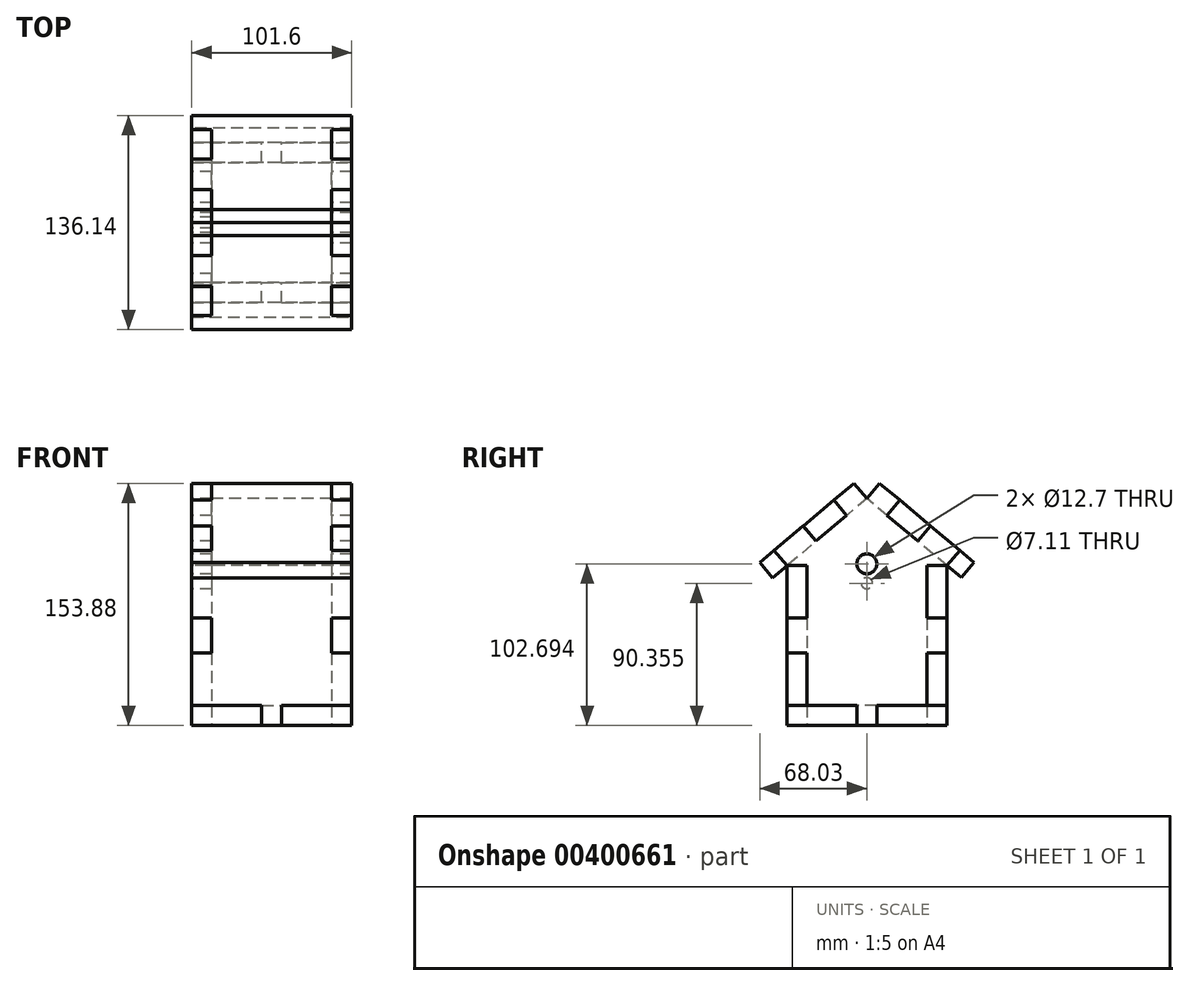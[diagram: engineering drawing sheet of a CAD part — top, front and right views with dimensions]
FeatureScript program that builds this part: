
annotation { "Feature Type Name" : "Feature", "Feature Type Description" : "" }
export const myFeature = defineFeature(function(context is Context, id is Id, definition is map)
    precondition{}
    {
        {
            var Q0;
            Q0=qCreatedBy(makeId("Top.planeOp"),FACE);
            var sketch = newSketch(context, id + "F0", { "sketchPlane" : qUnion([Q0])});
            skLineSegment(sketch, "E0.bottom", {"start": v(-50.8, 50.8) * mm, "end": v(-6.35, 50.8) * mm});
            skLineSegment(sketch, "E0.top", {"start": v(-50.8, -50.8) * mm, "end": v(-6.35, -50.8) * mm});
            skLineSegment(sketch, "E0.left", {"start": v(-50.8, 50.8) * mm, "end": v(-50.8, 6.35) * mm});
            skLineSegment(sketch, "E0.right", {"start": v(50.8, 50.8) * mm, "end": v(50.8, 6.35) * mm});
            skPoint(sketch, "E0.middle", {"position": v(0, 0) * mm});
            skLineSegment(sketch, "E1", {"start": v(-50.8, 6.35) * mm, "end": v(-38.1, 6.35) * mm});
            skLineSegment(sketch, "E2", {"start": v(-38.1, 6.35) * mm, "end": v(-38.1, -6.35) * mm});
            skLineSegment(sketch, "E3", {"start": v(-50.8, -6.35) * mm, "end": v(-38.1, -6.35) * mm});
            skLineSegment(sketch, "E4.trimOffspring", {"start": v(-50.8, -6.35) * mm, "end": v(-50.8, -50.8) * mm});
            skLineSegment(sketch, "E5.MirrorCS", {"start": v(50.8, 6.35) * mm, "end": v(38.1, 6.35) * mm});
            skLineSegment(sketch, "E6.MirrorCS", {"start": v(38.1, 6.35) * mm, "end": v(38.1, -6.35) * mm});
            skLineSegment(sketch, "E7.MirrorCS", {"start": v(50.8, -6.35) * mm, "end": v(38.1, -6.35) * mm});
            skLineSegment(sketch, "E8.trimOffspring", {"start": v(50.8, -6.35) * mm, "end": v(50.8, -50.8) * mm});
            skLineSegment(sketch, "E9", {"start": v(-6.35, 50.8) * mm, "end": v(-6.35, 38.1) * mm});
            skLineSegment(sketch, "E10", {"start": v(6.35, 50.8) * mm, "end": v(6.35, 38.1) * mm});
            skLineSegment(sketch, "E11", {"start": v(-6.35, 38.1) * mm, "end": v(6.35, 38.1) * mm});
            skLineSegment(sketch, "E12.trimOffspring", {"start": v(6.35, 50.8) * mm, "end": v(50.8, 50.8) * mm});
            skLineSegment(sketch, "E13.MirrorCS", {"start": v(-6.35, -38.1) * mm, "end": v(6.35, -38.1) * mm});
            skLineSegment(sketch, "E14.MirrorCS", {"start": v(-6.35, -50.8) * mm, "end": v(-6.35, -38.1) * mm});
            skLineSegment(sketch, "E15.MirrorCS", {"start": v(6.35, -50.8) * mm, "end": v(6.35, -38.1) * mm});
            skLineSegment(sketch, "E16.trimOffspring", {"start": v(6.35, -50.8) * mm, "end": v(50.8, -50.8) * mm});
            skSolve(sketch);
        }
        {
            var Q0;
            Q0 = qSketchRegion(id + "F0", true);
            extrude(context, id + "F1", {"entities" : qUnion([Q0]), "depth" : 12.7 * mm});
        }
        {
            var Q0;
            Q0=makeQuery(id+"F1.opExtrude","SWEPT_FACE",FACE,{"disambiguationData":[OSD([sQuery(id+"F0.wireOp",EDGE,"E12.trimOffspring")])]});
            var sketch = newSketch(context, id + "F2", { "sketchPlane" : qUnion([Q0])});
            skLineSegment(sketch, "E17.bottom", {"start": v(-6.35, 0) * mm, "end": v(6.35, 0) * mm});
            skLineSegment(sketch, "E17.top", {"start": v(-50.8, 101.6) * mm, "end": v(-12.84, 101.6) * mm});
            skLineSegment(sketch, "E17.right", {"start": v(50.8, 12.7) * mm, "end": v(50.8, 46.04) * mm});
            skLineSegment(sketch, "E18", {"start": v(-6.35, 0) * mm, "end": v(-6.35, 12.7) * mm});
            skLineSegment(sketch, "E19", {"start": v(6.35, 12.7) * mm, "end": v(6.35, 0) * mm});
            skLineSegment(sketch, "E20", {"start": v(51.45, 0) * mm, "end": v(-50.8, 0) * mm});
            skLineSegment(sketch, "E21", {"start": v(-50.8, 101.6) * mm, "end": v(-50.8, 68.26) * mm});
            skLineSegment(sketch, "E22", {"start": v(-50.8, 12.7) * mm, "end": v(-50.8, 46.04) * mm});
            skLineSegment(sketch, "E23", {"start": v(-50.8, 68.26) * mm, "end": v(-38.1, 68.26) * mm});
            skLineSegment(sketch, "E24", {"start": v(-38.1, 68.26) * mm, "end": v(-38.1, 46.04) * mm});
            skLineSegment(sketch, "E25", {"start": v(-50.8, 46.04) * mm, "end": v(-38.1, 46.04) * mm});
            skLineSegment(sketch, "E26.MirrorCS", {"start": v(50.8, 68.26) * mm, "end": v(38.1, 68.26) * mm});
            skLineSegment(sketch, "E27.MirrorCS", {"start": v(38.1, 68.26) * mm, "end": v(38.1, 46.04) * mm});
            skLineSegment(sketch, "E28.MirrorCS", {"start": v(50.8, 46.04) * mm, "end": v(38.1, 46.04) * mm});
            skLineSegment(sketch, "E29.trimOffspring", {"start": v(50.8, 68.26) * mm, "end": v(50.8, 101.6) * mm});
            skLineSegment(sketch, "E30", {"start": v(-50.8, 12.7) * mm, "end": v(-6.35, 12.7) * mm});
            skLineSegment(sketch, "E31", {"start": v(50.8, 12.7) * mm, "end": v(6.35, 12.7) * mm});
            skLineSegment(sketch, "E32", {"start": v(50.8, 101.6) * mm, "end": v(12.7, 101.6) * mm});
            skLineSegment(sketch, "E33", {"start": v(-12.84, 101.6) * mm, "end": v(-12.84, 88.9) * mm});
            skLineSegment(sketch, "E34", {"start": v(-12.84, 88.9) * mm, "end": v(12.7, 88.9) * mm});
            skLineSegment(sketch, "E35", {"start": v(12.7, 101.6) * mm, "end": v(12.7, 88.9) * mm});
            skLineSegment(sketch, "E36.trimOffspring", {"start": v(12.7, 101.6) * mm, "end": v(50.8, 101.6) * mm});
            skLineSegment(sketch, "E37", {"start": v(-12.84, 101.6) * mm, "end": v(12.7, 101.6) * mm});
            skSolve(sketch);
        }
        {
            var Q0;
            Q0 = qSketchRegion(id + "F2", true);
            var Q1;
            Q1=makeQuery(id+"F2.imprint","IMPRINT",FACE,{"disambiguationData":[TD([[makeQuery(id+"F2.imprint","IMPRINT",EDGE,{"derivedFrom":sQuery(id+"F2.wireOp",EDGE,"E17.top")}),-1.0]])]});
            extrude(context, id + "F3", {"entities" : qUnion([Q0, Q1]), "oppositeDirection" : true, "depth" : 12.7 * mm});
        }
        {
            var Q0;
            Q0=makeQuery(id+"F1.opExtrude","SWEPT_FACE",FACE,{"disambiguationData":[OSD([sQuery(id+"F0.wireOp",EDGE,"E4.trimOffspring")])]});
            var sketch = newSketch(context, id + "F4", { "sketchPlane" : qUnion([Q0])});
            skLineSegment(sketch, "E38", {"start": v(-38.1, 101.6) * mm, "end": v(-38.1, 68.26) * mm});
            skLineSegment(sketch, "E39", {"start": v(-50.8, 46.04) * mm, "end": v(-38.1, 46.04) * mm});
            skLineSegment(sketch, "E40", {"start": v(-38.1, 46.04) * mm, "end": v(-38.1, 12.7) * mm});
            skLineSegment(sketch, "E41", {"start": v(-38.1, 12.7) * mm, "end": v(-6.35, 12.7) * mm});
            skLineSegment(sketch, "E42", {"start": v(-6.35, 12.7) * mm, "end": v(-6.35, 0) * mm});
            skLineSegment(sketch, "E43", {"start": v(-6.35, 0) * mm, "end": v(6.35, 0) * mm});
            skLineSegment(sketch, "E44", {"start": v(6.35, 12.7) * mm, "end": v(6.35, 0) * mm});
            skLineSegment(sketch, "E45", {"start": v(6.35, 12.7) * mm, "end": v(50.8, 12.7) * mm});
            skLineSegment(sketch, "E46.MirrorCS", {"start": v(37.98, 68.26) * mm, "end": v(50.68, 68.26) * mm});
            skLineSegment(sketch, "E47.MirrorCS", {"start": v(50.8, 46.04) * mm, "end": v(38.1, 46.04) * mm});
            skLineSegment(sketch, "E48", {"start": v(38.1, 46.04) * mm, "end": v(38.1, 12.7) * mm});
            skLineSegment(sketch, "E49", {"start": v(-38.1, 68.26) * mm, "end": v(-38.1, 101.6) * mm});
            skLineSegment(sketch, "E50", {"start": v(-50.8, 68.26) * mm, "end": v(-38.1, 68.26) * mm});
            skLineSegment(sketch, "E51", {"start": v(-50.8, 68.26) * mm, "end": v(-50.8, 46.04) * mm});
            skLineSegment(sketch, "E52", {"start": v(50.8, 46.04) * mm, "end": v(50.68, 68.26) * mm});
            skLineSegment(sketch, "E53", {"start": v(38.1, 101.6) * mm, "end": v(37.98, 68.26) * mm});
            skCircle(sketch, "E54", {"center": v(0, 102.7) * mm, "radius": 6.35 * mm});
            skLineSegment(sketch, "E55", {"start": v(12.84, 133.39) * mm, "end": v(32.31, 117.08) * mm});
            skLineSegment(sketch, "E56.MirrorCS", {"start": v(-12.84, 133.39) * mm, "end": v(-32.31, 117.08) * mm});
            skLineSegment(sketch, "E57", {"start": v(38.1, 101.6) * mm, "end": v(50.8, 101.6) * mm});
            skLineSegment(sketch, "E58", {"start": v(-50.8, 101.6) * mm, "end": v(-38.1, 101.6) * mm});
            skLineSegment(sketch, "E59.0", {"start": v(-40.47, 126.82) * mm, "end": v(-58.95, 111.34) * mm});
            skLineSegment(sketch, "E59.1", {"start": v(-21, 143.13) * mm, "end": v(-8.15, 153.88) * mm});
            skLineSegment(sketch, "E59.2", {"start": v(21, 143.13) * mm, "end": v(8.15, 153.88) * mm});
            skLineSegment(sketch, "E59.3", {"start": v(40.47, 126.82) * mm, "end": v(58.95, 111.34) * mm});
            skLineSegment(sketch, "E60", {"start": v(-21, 143.13) * mm, "end": v(-12.84, 133.39) * mm});
            skLineSegment(sketch, "E61.0", {"start": v(-40.47, 126.82) * mm, "end": v(-32.31, 117.08) * mm});
            skLineSegment(sketch, "E62", {"start": v(-58.95, 111.34) * mm, "end": v(-50.8, 101.6) * mm});
            skLineSegment(sketch, "E63", {"start": v(0, 144.14) * mm, "end": v(-8.15, 153.88) * mm});
            skLineSegment(sketch, "E64.MirrorCS", {"start": v(0, 144.14) * mm, "end": v(8.15, 153.88) * mm});
            skLineSegment(sketch, "E65.MirrorCS", {"start": v(21, 143.13) * mm, "end": v(12.84, 133.39) * mm});
            skLineSegment(sketch, "E66.MirrorCS", {"start": v(40.47, 126.82) * mm, "end": v(32.31, 117.08) * mm});
            skLineSegment(sketch, "E67.MirrorCS", {"start": v(58.95, 111.34) * mm, "end": v(50.8, 101.6) * mm});
            skSolve(sketch);
        }
        {
            var Q0;
            Q0=makeQuery(id+"F4.imprint","IMPRINT",FACE,{"disambiguationData":[TD([[makeQuery(id+"F4.imprint","IMPRINT",EDGE,{"derivedFrom":sQuery(id+"F4.wireOp",EDGE,"E39")}),1.0]])]});
            extrude(context, id + "F5", {"entities" : qUnion([Q0]), "oppositeDirection" : true, "depth" : 12.7 * mm});
        }
        {
            var Q0;
            Q0=makeQuery(id+"F5.opExtrude","SWEPT_BODY",BODY,{"disambiguationData":[OSD([sQuery(id+"F4.wireOp",EDGE,"E38"),sQuery(id+"F4.wireOp",EDGE,"X9XSPmUe-CiWI-aoBv-T2po-TQAexjn7eybI"),sQuery(id+"F4.wireOp",EDGE,"dJrmhynW-Dqij-QMza-xG0c-FiWTCxEsIYWA"),sQuery(id+"F4.wireOp",EDGE,"E39"),sQuery(id+"F4.wireOp",EDGE,"E40"),sQuery(id+"F4.wireOp",EDGE,"E41"),sQuery(id+"F4.wireOp",EDGE,"E42"),sQuery(id+"F4.wireOp",EDGE,"E43"),sQuery(id+"F4.wireOp",EDGE,"E44"),sQuery(id+"F4.wireOp",EDGE,"E45"),sQuery(id+"F4.wireOp",EDGE,"E46.MirrorCS"),sQuery(id+"F4.wireOp",EDGE,"E47.MirrorCS"),sQuery(id+"F4.wireOp",EDGE,"7d2038e0-95e8-4499-a10f-d84e647bfb870.MirrorCS"),sQuery(id+"F4.wireOp",EDGE,"3vYFP86l-RaxW-OtnJ-uWa2-55M71DUzLll7"),sQuery(id+"F4.wireOp",EDGE,"E48"),sQuery(id+"F4.wireOp",EDGE,"Zbu0z1yX-9y8x-yxQX-ajQ6-gNSLApIAPJhn"),sQuery(id+"F4.wireOp",EDGE,"R7JFiNgy-TADh-oWcj-84EZ-rrNiW4IfCNvZ"),sQuery(id+"F4.wireOp",EDGE,"B0p03boq-Z1hu-uY6q-z4ZI-CZ741v1NlHqN"),sQuery(id+"F4.wireOp",EDGE,"oFCeFuHr-h53X-c4xK-BUlm-Z66OJnlluKQs"),sQuery(id+"F4.wireOp",EDGE,"795be2b4-63bf-446e-84a7-18ad7f5d247d.trimOffspring")])]});
            var Q1;
            Q1=makeQuery(id+"F5.opExtrude","CAP_VERTEX",VERTEX,{"disambiguationData":[OSD([sQuery(id+"F4.wireOp",EDGE,"E41"),sQuery(id+"F4.wireOp",EDGE,"E42")])],"isStart":false});
            var Q2;
            Q2=makeQuery(id+"F1.opExtrude","CAP_VERTEX",VERTEX,{"disambiguationData":[OSD([sQuery(id+"F0.wireOp",EDGE,"E0.right"),sQuery(id+"F0.wireOp",EDGE,"E5.MirrorCS")])],"isStart":false});
            transform(context, id + "F6", {"entities" : qUnion([Q0]), "transformType" : TransformType.TRANSLATION_ENTITY, "oppositeDirectionEntity" : false, "transformLine" : qUnion([Q1, Q2]), "makeCopy" : true});
        }
        {
            var Q0;
            Q0=makeQuery(id+"F3.opExtrude","SWEPT_BODY",BODY,{"disambiguationData":[OSD([sQuery(id+"F2.wireOp",EDGE,"E17.right"),sQuery(id+"F2.wireOp",EDGE,"E18"),sQuery(id+"F2.wireOp",EDGE,"E19"),sQuery(id+"F2.wireOp",EDGE,"E20"),sQuery(id+"F2.wireOp",EDGE,"E21"),sQuery(id+"F2.wireOp",EDGE,"E22"),sQuery(id+"F2.wireOp",EDGE,"E23"),sQuery(id+"F2.wireOp",EDGE,"E24"),sQuery(id+"F2.wireOp",EDGE,"E25"),sQuery(id+"F2.wireOp",EDGE,"E26.MirrorCS"),sQuery(id+"F2.wireOp",EDGE,"E27.MirrorCS"),sQuery(id+"F2.wireOp",EDGE,"E28.MirrorCS"),sQuery(id+"F2.wireOp",EDGE,"E29.trimOffspring"),sQuery(id+"F2.wireOp",EDGE,"E30"),sQuery(id+"F2.wireOp",EDGE,"E31"),sQuery(id+"F2.wireOp",EDGE,"E17.top"),sQuery(id+"F2.wireOp",EDGE,"E33"),sQuery(id+"F2.wireOp",EDGE,"E34"),sQuery(id+"F2.wireOp",EDGE,"E35"),sQuery(id+"F2.wireOp",EDGE,"E36.trimOffspring")])]});
            var Q1;
            Q1=makeQuery(id+"F1.opExtrude","CAP_VERTEX",VERTEX,{"disambiguationData":[OSD([sQuery(id+"F0.wireOp",EDGE,"E10"),sQuery(id+"F0.wireOp",EDGE,"E11")])],"isStart":false});
            var Q2;
            Q2=makeQuery(id+"F1.opExtrude","CAP_VERTEX",VERTEX,{"disambiguationData":[OSD([sQuery(id+"F0.wireOp",EDGE,"E15.MirrorCS"),sQuery(id+"F0.wireOp",EDGE,"E16.trimOffspring")])],"isStart":false});
            transform(context, id + "F7", {"entities" : qUnion([Q0]), "transformType" : TransformType.TRANSLATION_ENTITY, "oppositeDirectionEntity" : false, "transformLine" : qUnion([Q1, Q2]), "makeCopy" : true});
        }
        {
            var Q0;
            Q0=makeQuery(id+"F6.opPattern","COPY",FACE,{"derivedFrom":makeQuery(id+"F5.opExtrude","SWEPT_FACE",FACE,{"disambiguationData":[OSD([sQuery(id+"F4.wireOp",EDGE,"E56.MirrorCS")])]}),"instanceName":"1"});
            var sketch = newSketch(context, id + "F8", { "sketchPlane" : qUnion([Q0])});
            skLineSegment(sketch, "E68.bottom", {"start": v(50.8, -14.34) * mm, "end": v(-50.8, -14.34) * mm});
            skLineSegment(sketch, "E68.top", {"start": v(50.8, -92.54) * mm, "end": v(-50.8, -92.54) * mm});
            skLineSegment(sketch, "E68.left", {"start": v(50.8, -14.34) * mm, "end": v(50.8, -92.54) * mm});
            skLineSegment(sketch, "E68.right", {"start": v(-50.8, -14.34) * mm, "end": v(-50.8, -92.54) * mm});
            skSolve(sketch);
        }
        {
            var Q0;
            Q0 = qSketchRegion(id + "F8", true);
            extrude(context, id + "F9", {"entities" : qUnion([Q0]), "depth" : 12.7 * mm});
        }
        {
            var Q0;
            Q0=makeQuery(id+"F9.opExtrude","SWEPT_BODY",BODY,{"disambiguationData":[OSD([sQuery(id+"F8.wireOp",EDGE,"E68.bottom"),sQuery(id+"F8.wireOp",EDGE,"E68.top"),sQuery(id+"F8.wireOp",EDGE,"E68.left"),sQuery(id+"F8.wireOp",EDGE,"E68.right")])]});
            var Q1;
            Q1=sQuery(id+"F4.wireOp",EDGE,"E63");
            transform(context, id + "F10", {"entities" : qUnion([Q0]), "transformType" : TransformType.ROTATION, "transformAxis" : qUnion([Q1]), "angle" : 180 * degree, "makeCopy" : true});
        }
        {
            var Q0;
            Q0=makeQuery(id+"F10.opPattern","COPY",BODY,{"derivedFrom":makeQuery(id+"F9.opExtrude","SWEPT_BODY",BODY,{"disambiguationData":[OSD([sQuery(id+"F8.wireOp",EDGE,"E68.bottom"),sQuery(id+"F8.wireOp",EDGE,"E68.top"),sQuery(id+"F8.wireOp",EDGE,"E68.left"),sQuery(id+"F8.wireOp",EDGE,"E68.right")])]}),"instanceName":"1"});
            var Q1;
            Q1=makeQuery(id+"F10.opPattern","COPY",EDGE,{"derivedFrom":makeQuery(id+"F9.opExtrude","CAP_EDGE",EDGE,{"disambiguationData":[OSD([sQuery(id+"F8.wireOp",EDGE,"E68.top")])],"isStart":true}),"instanceName":"1"});
            transform(context, id + "F11", {"entities" : qUnion([Q0]), "transformType" : TransformType.ROTATION, "transformAxis" : qUnion([Q1]), "angle" : 80 * degree, "makeCopy" : false});
        }
        {
            var Q0;
            Q0=makeQuery(id+"F10.opPattern","COPY",BODY,{"derivedFrom":makeQuery(id+"F9.opExtrude","SWEPT_BODY",BODY,{"disambiguationData":[OSD([sQuery(id+"F8.wireOp",EDGE,"E68.bottom"),sQuery(id+"F8.wireOp",EDGE,"E68.top"),sQuery(id+"F8.wireOp",EDGE,"E68.left"),sQuery(id+"F8.wireOp",EDGE,"E68.right")])]}),"instanceName":"1"});
            var Q1;
            Q1=makeQuery(id+"F9.opExtrude","CAP_EDGE",EDGE,{"disambiguationData":[OSD([sQuery(id+"F8.wireOp",EDGE,"E68.top")])],"isStart":true});
            transform(context, id + "F12", {"entities" : qUnion([Q0]), "transformType" : TransformType.TRANSLATION_ENTITY, "oppositeDirectionEntity" : true, "transformLine" : qUnion([Q1]), "makeCopy" : false});
        }
        {
            var Q0;
            Q0=makeQuery(id+"F5.opExtrude","SWEPT_BODY",BODY,{"disambiguationData":[OSD([sQuery(id+"F4.wireOp",EDGE,"E39"),sQuery(id+"F4.wireOp",EDGE,"E40"),sQuery(id+"F4.wireOp",EDGE,"E41"),sQuery(id+"F4.wireOp",EDGE,"E42"),sQuery(id+"F4.wireOp",EDGE,"E43"),sQuery(id+"F4.wireOp",EDGE,"E44"),sQuery(id+"F4.wireOp",EDGE,"E45"),sQuery(id+"F4.wireOp",EDGE,"E46.MirrorCS"),sQuery(id+"F4.wireOp",EDGE,"E47.MirrorCS"),sQuery(id+"F4.wireOp",EDGE,"E48"),sQuery(id+"F4.wireOp",EDGE,"E49"),sQuery(id+"F4.wireOp",EDGE,"E50"),sQuery(id+"F4.wireOp",EDGE,"E51"),sQuery(id+"F4.wireOp",EDGE,"E52"),sQuery(id+"F4.wireOp",EDGE,"E53"),sQuery(id+"F4.wireOp",EDGE,"E54"),sQuery(id+"F4.wireOp",EDGE,"E55"),sQuery(id+"F4.wireOp",EDGE,"E56.MirrorCS"),sQuery(id+"F4.wireOp",EDGE,"E57"),sQuery(id+"F4.wireOp",EDGE,"E58"),sQuery(id+"F4.wireOp",EDGE,"E59.0"),sQuery(id+"F4.wireOp",EDGE,"E59.1"),sQuery(id+"F4.wireOp",EDGE,"E59.2"),sQuery(id+"F4.wireOp",EDGE,"E59.3"),sQuery(id+"F4.wireOp",EDGE,"E60"),sQuery(id+"F4.wireOp",EDGE,"E61.0"),sQuery(id+"F4.wireOp",EDGE,"E62"),sQuery(id+"F4.wireOp",EDGE,"E63"),sQuery(id+"F4.wireOp",EDGE,"E64.MirrorCS"),sQuery(id+"F4.wireOp",EDGE,"E65.MirrorCS"),sQuery(id+"F4.wireOp",EDGE,"E66.MirrorCS"),sQuery(id+"F4.wireOp",EDGE,"E67.MirrorCS")])]});
            var Q1;
            Q1=makeQuery(id+"F9.opExtrude","SWEPT_BODY",BODY,{"disambiguationData":[OSD([sQuery(id+"F8.wireOp",EDGE,"E68.bottom"),sQuery(id+"F8.wireOp",EDGE,"E68.top"),sQuery(id+"F8.wireOp",EDGE,"E68.left"),sQuery(id+"F8.wireOp",EDGE,"E68.right")])]});
            booleanBodies(context, id + "F13", {"operationType" : BooleanOperationType.SUBTRACTION, "tools" : qUnion([Q0]), "targets" : qUnion([Q1]), "keepTools" : true});
        }
        {
            var Q0;
            Q0=makeQuery(id+"F6.opPattern","COPY",BODY,{"derivedFrom":makeQuery(id+"F5.opExtrude","SWEPT_BODY",BODY,{"disambiguationData":[OSD([sQuery(id+"F4.wireOp",EDGE,"E39"),sQuery(id+"F4.wireOp",EDGE,"E40"),sQuery(id+"F4.wireOp",EDGE,"E41"),sQuery(id+"F4.wireOp",EDGE,"E42"),sQuery(id+"F4.wireOp",EDGE,"E43"),sQuery(id+"F4.wireOp",EDGE,"E44"),sQuery(id+"F4.wireOp",EDGE,"E45"),sQuery(id+"F4.wireOp",EDGE,"E46.MirrorCS"),sQuery(id+"F4.wireOp",EDGE,"E47.MirrorCS"),sQuery(id+"F4.wireOp",EDGE,"E48"),sQuery(id+"F4.wireOp",EDGE,"E49"),sQuery(id+"F4.wireOp",EDGE,"E50"),sQuery(id+"F4.wireOp",EDGE,"E51"),sQuery(id+"F4.wireOp",EDGE,"E52"),sQuery(id+"F4.wireOp",EDGE,"E53"),sQuery(id+"F4.wireOp",EDGE,"E54"),sQuery(id+"F4.wireOp",EDGE,"E55"),sQuery(id+"F4.wireOp",EDGE,"E56.MirrorCS"),sQuery(id+"F4.wireOp",EDGE,"E57"),sQuery(id+"F4.wireOp",EDGE,"E58"),sQuery(id+"F4.wireOp",EDGE,"E59.0"),sQuery(id+"F4.wireOp",EDGE,"E59.1"),sQuery(id+"F4.wireOp",EDGE,"E59.2"),sQuery(id+"F4.wireOp",EDGE,"E59.3"),sQuery(id+"F4.wireOp",EDGE,"E60"),sQuery(id+"F4.wireOp",EDGE,"E61.0"),sQuery(id+"F4.wireOp",EDGE,"E62"),sQuery(id+"F4.wireOp",EDGE,"E63"),sQuery(id+"F4.wireOp",EDGE,"E64.MirrorCS"),sQuery(id+"F4.wireOp",EDGE,"E65.MirrorCS"),sQuery(id+"F4.wireOp",EDGE,"E66.MirrorCS"),sQuery(id+"F4.wireOp",EDGE,"E67.MirrorCS")])]}),"instanceName":"1"});
            var Q1;
            Q1=makeQuery(id+"F5.opExtrude","SWEPT_BODY",BODY,{"disambiguationData":[OSD([sQuery(id+"F4.wireOp",EDGE,"E39"),sQuery(id+"F4.wireOp",EDGE,"E40"),sQuery(id+"F4.wireOp",EDGE,"E41"),sQuery(id+"F4.wireOp",EDGE,"E42"),sQuery(id+"F4.wireOp",EDGE,"E43"),sQuery(id+"F4.wireOp",EDGE,"E44"),sQuery(id+"F4.wireOp",EDGE,"E45"),sQuery(id+"F4.wireOp",EDGE,"E46.MirrorCS"),sQuery(id+"F4.wireOp",EDGE,"E47.MirrorCS"),sQuery(id+"F4.wireOp",EDGE,"E48"),sQuery(id+"F4.wireOp",EDGE,"E49"),sQuery(id+"F4.wireOp",EDGE,"E50"),sQuery(id+"F4.wireOp",EDGE,"E51"),sQuery(id+"F4.wireOp",EDGE,"E52"),sQuery(id+"F4.wireOp",EDGE,"E53"),sQuery(id+"F4.wireOp",EDGE,"E54"),sQuery(id+"F4.wireOp",EDGE,"E55"),sQuery(id+"F4.wireOp",EDGE,"E56.MirrorCS"),sQuery(id+"F4.wireOp",EDGE,"E57"),sQuery(id+"F4.wireOp",EDGE,"E58"),sQuery(id+"F4.wireOp",EDGE,"E59.0"),sQuery(id+"F4.wireOp",EDGE,"E59.1"),sQuery(id+"F4.wireOp",EDGE,"E59.2"),sQuery(id+"F4.wireOp",EDGE,"E59.3"),sQuery(id+"F4.wireOp",EDGE,"E60"),sQuery(id+"F4.wireOp",EDGE,"E61.0"),sQuery(id+"F4.wireOp",EDGE,"E62"),sQuery(id+"F4.wireOp",EDGE,"E63"),sQuery(id+"F4.wireOp",EDGE,"E64.MirrorCS"),sQuery(id+"F4.wireOp",EDGE,"E65.MirrorCS"),sQuery(id+"F4.wireOp",EDGE,"E66.MirrorCS"),sQuery(id+"F4.wireOp",EDGE,"E67.MirrorCS")])]});
            var Q2;
            Q2=makeQuery(id+"F10.opPattern","COPY",BODY,{"derivedFrom":makeQuery(id+"F9.opExtrude","SWEPT_BODY",BODY,{"disambiguationData":[OSD([sQuery(id+"F8.wireOp",EDGE,"E68.bottom"),sQuery(id+"F8.wireOp",EDGE,"E68.top"),sQuery(id+"F8.wireOp",EDGE,"E68.left"),sQuery(id+"F8.wireOp",EDGE,"E68.right")])]}),"instanceName":"1"});
            booleanBodies(context, id + "F14", {"operationType" : BooleanOperationType.SUBTRACTION, "tools" : qUnion([Q0, Q1]), "targets" : qUnion([Q2]), "keepTools" : true});
        }
        {
            var Q0;
            Q0=makeQuery(id+"F4.imprint","IMPRINT",FACE,{"disambiguationData":[TD([[makeQuery(id+"F4.imprint","IMPRINT",EDGE,{"derivedFrom":sQuery(id+"F4.wireOp",EDGE,"E39")}),1.0]])]});
            var sketch = newSketch(context, id + "F15", { "sketchPlane" : qUnion([Q0])});
            skCircle(sketch, "E69", {"center": v(0, 90.36) * mm, "radius": 3.56 * mm});
            skSolve(sketch);
        }
        {
            var Q0;
            Q0 = qSketchRegion(id + "F15", true);
            extrude(context, id + "F16", {"entities" : qUnion([Q0]), "operationType" : NewBodyOperationType.REMOVE, "oppositeDirection" : true, "depth" : 25.4 * mm});
        }
        {
            var Q0;
            Q0=makeQuery(id+"F6.opPattern","COPY",BODY,{"derivedFrom":makeQuery(id+"F5.opExtrude","SWEPT_BODY",BODY,{"disambiguationData":[OSD([sQuery(id+"F4.wireOp",EDGE,"E39"),sQuery(id+"F4.wireOp",EDGE,"E40"),sQuery(id+"F4.wireOp",EDGE,"E41"),sQuery(id+"F4.wireOp",EDGE,"E42"),sQuery(id+"F4.wireOp",EDGE,"E43"),sQuery(id+"F4.wireOp",EDGE,"E44"),sQuery(id+"F4.wireOp",EDGE,"E45"),sQuery(id+"F4.wireOp",EDGE,"E46.MirrorCS"),sQuery(id+"F4.wireOp",EDGE,"E47.MirrorCS"),sQuery(id+"F4.wireOp",EDGE,"E48"),sQuery(id+"F4.wireOp",EDGE,"E49"),sQuery(id+"F4.wireOp",EDGE,"E50"),sQuery(id+"F4.wireOp",EDGE,"E51"),sQuery(id+"F4.wireOp",EDGE,"E52"),sQuery(id+"F4.wireOp",EDGE,"E53"),sQuery(id+"F4.wireOp",EDGE,"E54"),sQuery(id+"F4.wireOp",EDGE,"E55"),sQuery(id+"F4.wireOp",EDGE,"E56.MirrorCS"),sQuery(id+"F4.wireOp",EDGE,"E57"),sQuery(id+"F4.wireOp",EDGE,"E58"),sQuery(id+"F4.wireOp",EDGE,"E59.0"),sQuery(id+"F4.wireOp",EDGE,"E59.1"),sQuery(id+"F4.wireOp",EDGE,"E59.2"),sQuery(id+"F4.wireOp",EDGE,"E59.3"),sQuery(id+"F4.wireOp",EDGE,"E60"),sQuery(id+"F4.wireOp",EDGE,"E61.0"),sQuery(id+"F4.wireOp",EDGE,"E62"),sQuery(id+"F4.wireOp",EDGE,"E63"),sQuery(id+"F4.wireOp",EDGE,"E64.MirrorCS"),sQuery(id+"F4.wireOp",EDGE,"E65.MirrorCS"),sQuery(id+"F4.wireOp",EDGE,"E66.MirrorCS"),sQuery(id+"F4.wireOp",EDGE,"E67.MirrorCS")])]}),"instanceName":"1"});
            var Q1;
            Q1=makeQuery(id+"F9.opExtrude","SWEPT_BODY",BODY,{"disambiguationData":[OSD([sQuery(id+"F8.wireOp",EDGE,"E68.bottom"),sQuery(id+"F8.wireOp",EDGE,"E68.top"),sQuery(id+"F8.wireOp",EDGE,"E68.left"),sQuery(id+"F8.wireOp",EDGE,"E68.right")])]});
            booleanBodies(context, id + "F17", {"operationType" : BooleanOperationType.SUBTRACTION, "tools" : qUnion([Q0]), "targets" : qUnion([Q1]), "keepTools" : true});
        }
    });
